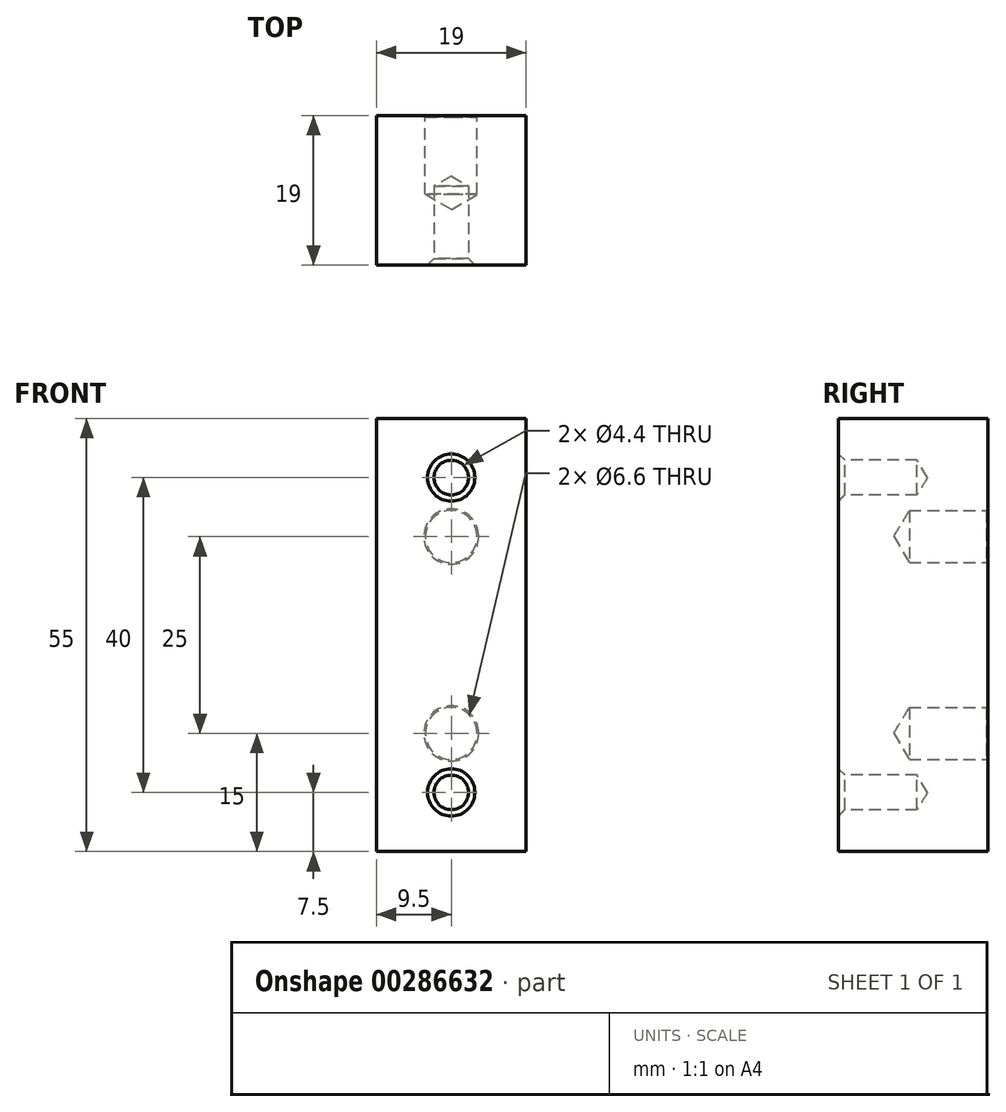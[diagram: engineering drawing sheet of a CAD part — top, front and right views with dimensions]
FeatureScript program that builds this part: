
annotation { "Feature Type Name" : "Feature", "Feature Type Description" : "" }
export const myFeature = defineFeature(function(context is Context, id is Id, definition is map)
    precondition{}
    {
        {
            var Q0;
            Q0=qCreatedBy(makeId("Front.planeOp"),FACE);
            var sketch = newSketch(context, id + "F0", { "sketchPlane" : qUnion([Q0])});
            skLineSegment(sketch, "E0.bottom", {"start": v(0, 0) * mm, "end": v(19, 0) * mm});
            skLineSegment(sketch, "E0.top", {"start": v(0, -55) * mm, "end": v(19, -55) * mm});
            skLineSegment(sketch, "E0.left", {"start": v(0, 0) * mm, "end": v(0, -55) * mm});
            skLineSegment(sketch, "E0.right", {"start": v(19, 0) * mm, "end": v(19, -55) * mm});
            skSolve(sketch);
        }
        {
            var Q0;
            Q0=makeQuery(id+"F0.imprint","IMPRINT",FACE,{"disambiguationData":[TD([[makeQuery(id+"F0.imprint","IMPRINT",EDGE,{"derivedFrom":sQuery(id+"F0.wireOp",EDGE,"E0.bottom")}),-1.0]])]});
            extrude(context, id + "F1", {"entities" : qUnion([Q0]), "depth" : 19 * mm});
        }
        {
            var Q0;
            Q0=makeQuery(id+"F1.opExtrude","CAP_FACE",FACE,{"disambiguationData":[OSD([sQuery(id+"F0.wireOp",EDGE,"E0.bottom"),sQuery(id+"F0.wireOp",EDGE,"E0.top"),sQuery(id+"F0.wireOp",EDGE,"E0.left"),sQuery(id+"F0.wireOp",EDGE,"E0.right")])],"isStart":false});
            var sketch = newSketch(context, id + "F2", { "sketchPlane" : qUnion([Q0])});
            skPoint(sketch, "E1", {"position": v(9.5, -7.5) * mm});
            skPoint(sketch, "E1.positionSnap0", {"position": v(9.5, 0) * mm});
            skPoint(sketch, "E2", {"position": v(9.5, -47.5) * mm});
            skSolve(sketch);
        }
        {
            var Q0;
            Q0=sQuery(id+"F2.wireOp",VERTEX,"E1");
            var Q1;
            Q1=sQuery(id+"F2.wireOp",VERTEX,"E2");
            var Q2;
            Q2=makeQuery(id+"F1.opExtrude","SWEPT_BODY",BODY,{"disambiguationData":[OSD([sQuery(id+"F0.wireOp",EDGE,"E0.bottom"),sQuery(id+"F0.wireOp",EDGE,"E0.top"),sQuery(id+"F0.wireOp",EDGE,"E0.left"),sQuery(id+"F0.wireOp",EDGE,"E0.right")])]});
            hole(context, id + "F3", {"style" : HoleStyle.C_SINK, "endStyle" : HoleEndStyle.BLIND, "holeDiameter" : 4.4 * mm, "cSinkDiameter" : 6 * mm, "cSinkAngle" : 90 * degree, "holeDepth" : 10 * mm, "tappedDepth" : 50 * mm, "tapClearance" : 3, "locations" : qUnion([Q0, Q1]), "scope" : qUnion([Q2])});
        }
        {
            var Q0;
            Q0=makeQuery(id+"F1.opExtrude","CAP_FACE",FACE,{"disambiguationData":[OSD([sQuery(id+"F0.wireOp",EDGE,"E0.bottom"),sQuery(id+"F0.wireOp",EDGE,"E0.top"),sQuery(id+"F0.wireOp",EDGE,"E0.left"),sQuery(id+"F0.wireOp",EDGE,"E0.right")])],"isStart":true});
            var sketch = newSketch(context, id + "F4", { "sketchPlane" : qUnion([Q0])});
            skPoint(sketch, "E3", {"position": v(-9.5, 0) * mm});
            skPoint(sketch, "E4", {"position": v(-9.5, -15) * mm});
            skPoint(sketch, "E5", {"position": v(-9.5, -40) * mm});
            skSolve(sketch);
        }
        {
            var Q0;
            Q0=sQuery(id+"F4.wireOp",VERTEX,"E4");
            var Q1;
            Q1=sQuery(id+"F4.wireOp",VERTEX,"E5");
            var Q2;
            Q2=makeQuery(id+"F1.opExtrude","SWEPT_BODY",BODY,{"disambiguationData":[OSD([sQuery(id+"F0.wireOp",EDGE,"E0.bottom"),sQuery(id+"F0.wireOp",EDGE,"E0.top"),sQuery(id+"F0.wireOp",EDGE,"E0.left"),sQuery(id+"F0.wireOp",EDGE,"E0.right")])]});
            hole(context, id + "F5", {"style" : HoleStyle.C_SINK, "endStyle" : HoleEndStyle.BLIND, "holeDiameter" : 6.6 * mm, "cSinkDiameter" : 7 * mm, "cSinkAngle" : 90 * degree, "holeDepth" : 10 * mm, "tappedDepth" : 50 * mm, "tapClearance" : 3, "locations" : qUnion([Q0, Q1]), "scope" : qUnion([Q2])});
        }
    });
